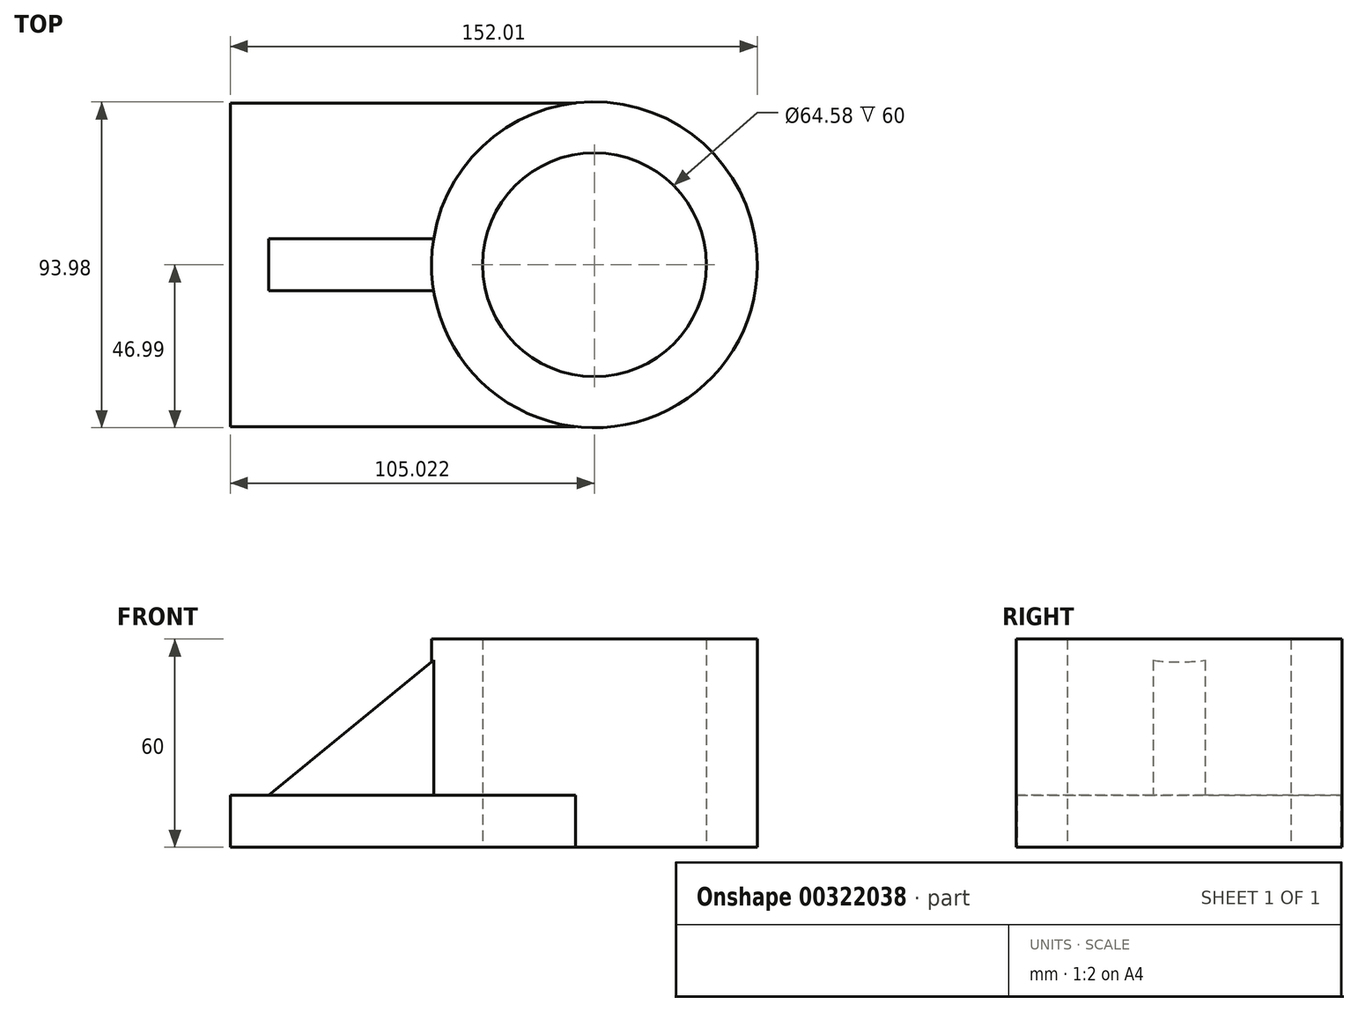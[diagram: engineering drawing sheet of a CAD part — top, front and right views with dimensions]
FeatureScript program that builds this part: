
annotation { "Feature Type Name" : "Feature", "Feature Type Description" : "" }
export const myFeature = defineFeature(function(context is Context, id is Id, definition is map)
    precondition{}
    {
        {
            var Q0;
            Q0=qCreatedBy(makeId("Top.planeOp"),FACE);
            var sketch = newSketch(context, id + "F0", { "sketchPlane" : qUnion([Q0])});
            skCircle(sketch, "E0", {"center": v(50.2, 0) * mm, "radius": 32.3 * mm});
            skCircle(sketch, "E1", {"center": v(50.2, 0) * mm, "radius": 47 * mm});
            skSolve(sketch);
        }
        {
            var Q0;
            Q0 = qSketchRegion(id + "F0", true);
            extrude(context, id + "F1", {"entities" : qUnion([Q0]), "depth" : 60 * mm});
        }
        {
            var Q0;
            Q0=makeQuery(id+"F1.opExtrude","CAP_FACE",FACE,{"disambiguationData":[OSD([sQuery(id+"F0.wireOp",EDGE,"E0"),sQuery(id+"F0.wireOp",EDGE,"E1")])],"isStart":true});
            var sketch = newSketch(context, id + "F2", { "sketchPlane" : qUnion([Q0])});
            skLineSegment(sketch, "E2.bottom", {"start": v(44.8, 46.68) * mm, "end": v(-54.82, 46.68) * mm});
            skLineSegment(sketch, "E2.top", {"start": v(44.8, -46.68) * mm, "end": v(-54.82, -46.68) * mm});
            skLineSegment(sketch, "E2.right", {"start": v(-54.82, 46.68) * mm, "end": v(-54.82, -46.68) * mm});
            skPoint(sketch, "E2.middle", {"position": v(-5.01, 0) * mm});
            skArc(sketch, "E3.0", {"start": v(44.8, 46.68) * mm, "mid": v(3.21, 0) * mm, "end": v(44.8, -46.68) * mm});
            skSolve(sketch);
        }
        {
            var Q0;
            {var subQ0=sQuery(id+"F2.wireOp",EDGE,"E2.bottom");Q0=makeQuery(id+"F2.imprint","IMPRINT",FACE,{"disambiguationData":[TD([[makeQuery(id+"F2.imprint","IMPRINT",EDGE,{"derivedFrom":subQ0}),1.0]])]});}
            extrude(context, id + "F3", {"entities" : qUnion([Q0]), "operationType" : NewBodyOperationType.ADD, "oppositeDirection" : true, "offsetDistance" : 25 * mm, "depth" : 15 * mm});
        }
        {
            var Q0;
            Q0=qCreatedBy(makeId("Front.planeOp"),FACE);
            var sketch = newSketch(context, id + "F4", { "sketchPlane" : qUnion([Q0])});
            skLineSegment(sketch, "E4", {"start": v(-44.18, 14.62) * mm, "end": v(4.08, 14.62) * mm});
            skLineSegment(sketch, "E5", {"start": v(4.08, 14.62) * mm, "end": v(4.08, 54.14) * mm});
            skLineSegment(sketch, "E6", {"start": v(4.08, 54.14) * mm, "end": v(-44.18, 14.62) * mm});
            skSolve(sketch);
        }
        {
            var Q0;
            Q0 = qSketchRegion(id + "F4", true);
            extrude(context, id + "F5", {"entities" : qUnion([Q0]), "operationType" : NewBodyOperationType.ADD, "endBound" : BoundingType.SYMMETRIC, "offsetDistance" : 25 * mm, "depth" : 15 * mm});
        }
    });
